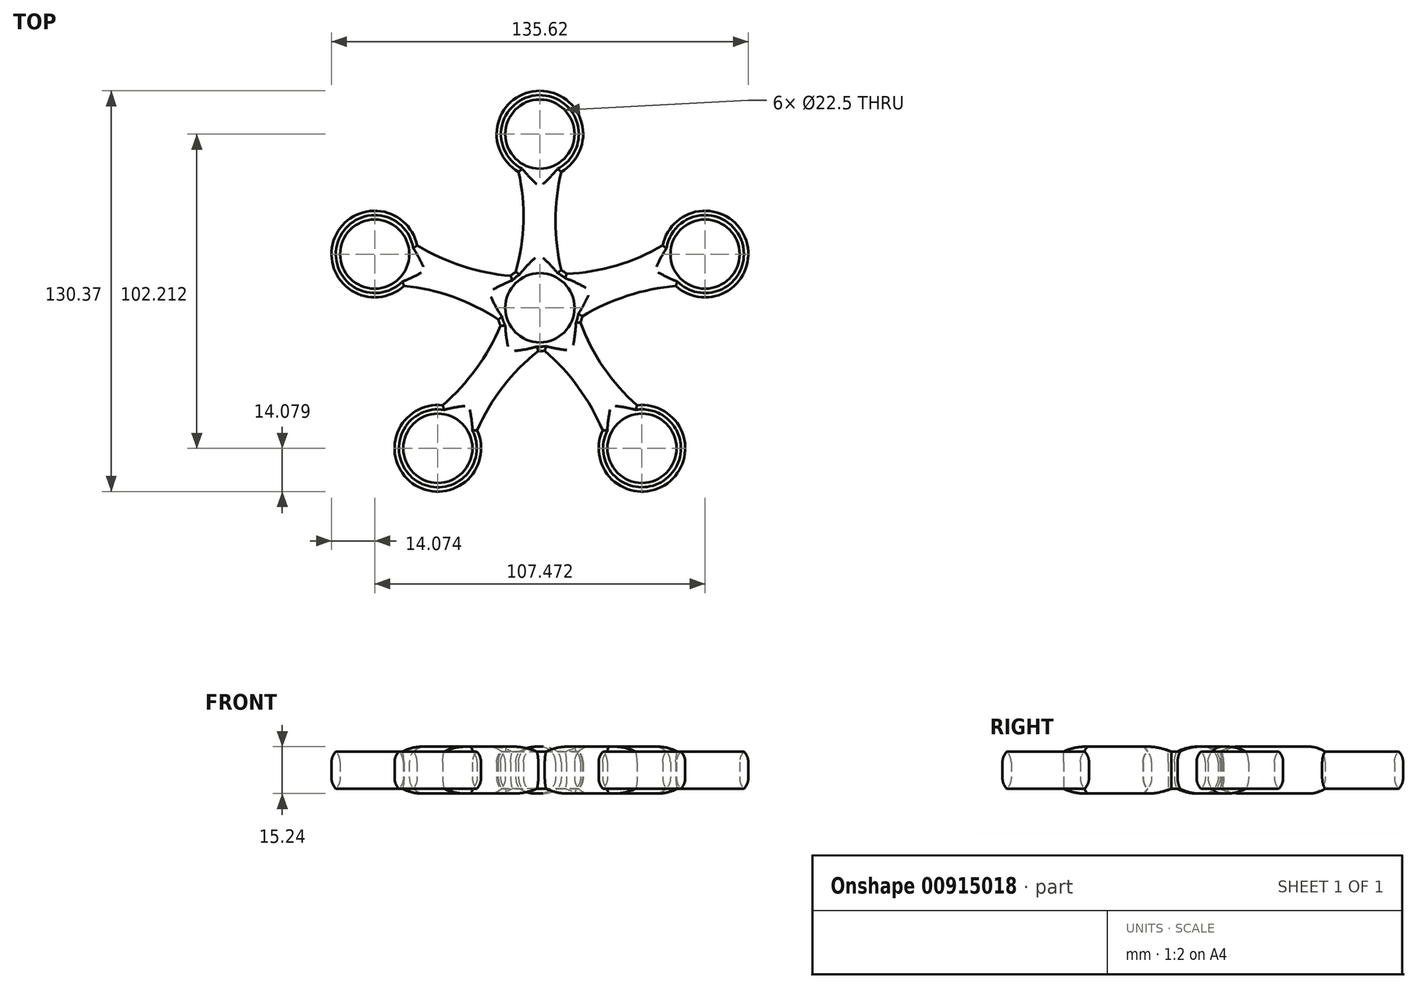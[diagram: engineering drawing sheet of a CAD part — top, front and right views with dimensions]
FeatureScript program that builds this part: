
annotation { "Feature Type Name" : "Feature", "Feature Type Description" : "" }
export const myFeature = defineFeature(function(context is Context, id is Id, definition is map)
    precondition{}
    {
        {
            var Q0;
            Q0=qCreatedBy(makeId("Top.planeOp"),FACE);
            var sketch = newSketch(context, id + "F0", { "sketchPlane" : qUnion([Q0])});
            skCircle(sketch, "E0", {"center": v(0, 0) * mm, "radius": 11.25 * mm});
            skCircle(sketch, "E1", {"center": v(0, 56.5) * mm, "radius": 11.25 * mm});
            skArc(sketch, "E2", {"start": v(6.94, 44.25) * mm, "mid": v(0, 70.58) * mm, "end": v(-6.94, 44.25) * mm});
            skArc(sketch, "E3", {"start": v(-7.84, 11.7) * mm, "mid": v(0.53, -14.07) * mm, "end": v(6.94, 12.25) * mm});
            skArc(sketch, "E4", {"start": v(-7.84, 11.7) * mm, "mid": v(-5.37, 27.92) * mm, "end": v(-6.94, 44.25) * mm});
            skArc(sketch, "E5", {"start": v(6.94, 44.25) * mm, "mid": v(5.1, 28.25) * mm, "end": v(6.94, 12.25) * mm});
            skArc(sketch, "E6.1.0", {"start": v(-39.94, 20.28) * mm, "mid": v(-67.12, 21.8) * mm, "end": v(-44.23, 7.07) * mm});
            skCircle(sketch, "E6.1.1", {"center": v(-53.74, 17.46) * mm, "radius": 11.25 * mm});
            skArc(sketch, "E6.1.2", {"start": v(-13.54, -3.84) * mm, "mid": v(-28.2, 3.52) * mm, "end": v(-44.23, 7.07) * mm});
            skArc(sketch, "E6.1.3", {"start": v(-39.94, 20.28) * mm, "mid": v(-25.3, 13.58) * mm, "end": v(-9.5, 10.39) * mm});
            skArc(sketch, "E6.2.0", {"start": v(-31.63, -31.72) * mm, "mid": v(-41.48, -57.1) * mm, "end": v(-20.4, -39.88) * mm});
            skCircle(sketch, "E6.2.1", {"center": v(-33.21, -45.71) * mm, "radius": 11.25 * mm});
            skArc(sketch, "E6.2.2", {"start": v(-0.53, -14.07) * mm, "mid": v(-12.07, -25.74) * mm, "end": v(-20.4, -39.88) * mm});
            skArc(sketch, "E6.2.3", {"start": v(-31.63, -31.72) * mm, "mid": v(-20.73, -19.86) * mm, "end": v(-12.81, -5.83) * mm});
            skArc(sketch, "E6.3.0", {"start": v(20.4, -39.88) * mm, "mid": v(41.48, -57.1) * mm, "end": v(31.63, -31.72) * mm});
            skCircle(sketch, "E6.3.1", {"center": v(33.21, -45.71) * mm, "radius": 11.25 * mm});
            skArc(sketch, "E6.3.2", {"start": v(13.21, -4.85) * mm, "mid": v(20.75, -19.43) * mm, "end": v(31.63, -31.72) * mm});
            skArc(sketch, "E6.3.3", {"start": v(20.4, -39.88) * mm, "mid": v(12.48, -25.85) * mm, "end": v(1.58, -13.99) * mm});
            skArc(sketch, "E6.4.0", {"start": v(44.23, 7.07) * mm, "mid": v(67.12, 21.8) * mm, "end": v(39.94, 20.28) * mm});
            skCircle(sketch, "E6.4.1", {"center": v(53.74, 17.46) * mm, "radius": 11.25 * mm});
            skArc(sketch, "E6.4.2", {"start": v(8.7, 11.07) * mm, "mid": v(24.9, 13.73) * mm, "end": v(39.94, 20.28) * mm});
            skArc(sketch, "E6.4.3", {"start": v(44.23, 7.07) * mm, "mid": v(28.44, 3.88) * mm, "end": v(13.8, -2.82) * mm});
            skSolve(sketch);
        }
        {
            var Q0;
            Q0=makeQuery(id+"F0.imprint","IMPRINT",FACE,{"disambiguationData":[TD([[makeQuery(id+"F0.imprint","IMPRINT",EDGE,{"derivedFrom":sQuery(id+"F0.wireOp",EDGE,"E6.1.0")}),1.0]])]});
            var Q1;
            Q1=makeQuery(id+"F0.imprint","IMPRINT",FACE,{"disambiguationData":[TD([[makeQuery(id+"F0.imprint","IMPRINT",EDGE,{"derivedFrom":sQuery(id+"F0.wireOp",EDGE,"E0")}),-1.0]])]});
            var Q2;
            Q2=makeQuery(id+"F0.imprint","IMPRINT",FACE,{"disambiguationData":[TD([[makeQuery(id+"F0.imprint","IMPRINT",EDGE,{"derivedFrom":sQuery(id+"F0.wireOp",EDGE,"E6.4.0")}),1.0]])]});
            var Q3;
            Q3=makeQuery(id+"F0.imprint","IMPRINT",FACE,{"disambiguationData":[TD([[makeQuery(id+"F0.imprint","IMPRINT",EDGE,{"derivedFrom":sQuery(id+"F0.wireOp",EDGE,"E6.3.0")}),1.0]])]});
            var Q4;
            Q4=makeQuery(id+"F0.imprint","IMPRINT",FACE,{"disambiguationData":[TD([[makeQuery(id+"F0.imprint","IMPRINT",EDGE,{"derivedFrom":sQuery(id+"F0.wireOp",EDGE,"E6.2.0")}),1.0]])]});
            extrude(context, id + "F1", {"entities" : qUnion([Q0, Q1, Q2, Q3, Q4]), "depth" : 15.24 * mm, "offsetDistance" : 25.4 * mm});
        }
        {
            var Q0;
            Q0=makeQuery(id+"F1.opExtrude","CAP_FACE",FACE,{"disambiguationData":[OSD([sQuery(id+"F0.wireOp",EDGE,"E0"),sQuery(id+"F0.wireOp",EDGE,"E1"),sQuery(id+"F0.wireOp",EDGE,"E2"),sQuery(id+"F0.wireOp",EDGE,"E3"),sQuery(id+"F0.wireOp",EDGE,"E4"),sQuery(id+"F0.wireOp",EDGE,"E5"),sQuery(id+"F0.wireOp",EDGE,"E6.1.0"),sQuery(id+"F0.wireOp",EDGE,"E6.1.1"),sQuery(id+"F0.wireOp",EDGE,"E6.1.2"),sQuery(id+"F0.wireOp",EDGE,"E6.1.3"),sQuery(id+"F0.wireOp",EDGE,"E6.2.0"),sQuery(id+"F0.wireOp",EDGE,"E6.2.1"),sQuery(id+"F0.wireOp",EDGE,"E6.2.2"),sQuery(id+"F0.wireOp",EDGE,"E6.2.3"),sQuery(id+"F0.wireOp",EDGE,"E6.3.0"),sQuery(id+"F0.wireOp",EDGE,"E6.3.1"),sQuery(id+"F0.wireOp",EDGE,"E6.3.2"),sQuery(id+"F0.wireOp",EDGE,"E6.3.3"),sQuery(id+"F0.wireOp",EDGE,"E6.4.0"),sQuery(id+"F0.wireOp",EDGE,"E6.4.1"),sQuery(id+"F0.wireOp",EDGE,"E6.4.2"),sQuery(id+"F0.wireOp",EDGE,"E6.4.3")])],"isStart":false});
            fillet(context, id + "F2", {"entities" : qUnion([Q0]), "radius" : 5.08 * mm, "tangentPropagation" : true, "allowEdgeOverflow" : false});
        }
        {
            var Q0;
            Q0=makeQuery(id+"F1.opExtrude","CAP_FACE",FACE,{"disambiguationData":[OSD([sQuery(id+"F0.wireOp",EDGE,"E0"),sQuery(id+"F0.wireOp",EDGE,"E1"),sQuery(id+"F0.wireOp",EDGE,"E2"),sQuery(id+"F0.wireOp",EDGE,"E3"),sQuery(id+"F0.wireOp",EDGE,"E4"),sQuery(id+"F0.wireOp",EDGE,"E5"),sQuery(id+"F0.wireOp",EDGE,"E6.1.0"),sQuery(id+"F0.wireOp",EDGE,"E6.1.1"),sQuery(id+"F0.wireOp",EDGE,"E6.1.2"),sQuery(id+"F0.wireOp",EDGE,"E6.1.3"),sQuery(id+"F0.wireOp",EDGE,"E6.2.0"),sQuery(id+"F0.wireOp",EDGE,"E6.2.1"),sQuery(id+"F0.wireOp",EDGE,"E6.2.2"),sQuery(id+"F0.wireOp",EDGE,"E6.2.3"),sQuery(id+"F0.wireOp",EDGE,"E6.3.0"),sQuery(id+"F0.wireOp",EDGE,"E6.3.1"),sQuery(id+"F0.wireOp",EDGE,"E6.3.2"),sQuery(id+"F0.wireOp",EDGE,"E6.3.3"),sQuery(id+"F0.wireOp",EDGE,"E6.4.0"),sQuery(id+"F0.wireOp",EDGE,"E6.4.1"),sQuery(id+"F0.wireOp",EDGE,"E6.4.2"),sQuery(id+"F0.wireOp",EDGE,"E6.4.3")])],"isStart":true});
            fillet(context, id + "F3", {"entities" : qUnion([Q0]), "radius" : 5.08 * mm, "tangentPropagation" : true, "allowEdgeOverflow" : false});
        }
    });
